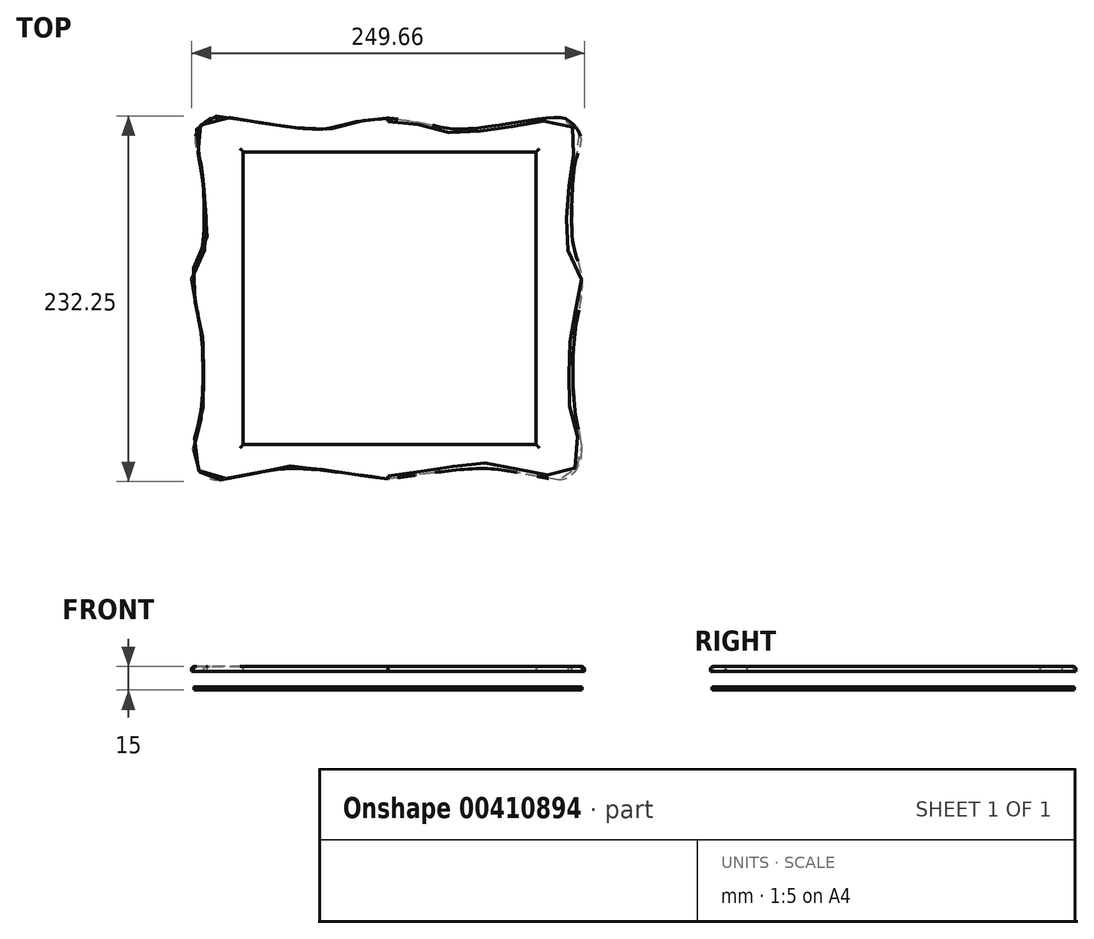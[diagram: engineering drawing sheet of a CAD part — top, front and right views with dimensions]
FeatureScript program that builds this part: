
annotation { "Feature Type Name" : "Feature", "Feature Type Description" : "" }
export const myFeature = defineFeature(function(context is Context, id is Id, definition is map)
    precondition{}
    {
        {
            var Q0;
            Q0=qCreatedBy(makeId("Top.planeOp"),FACE);
            var sketch = newSketch(context, id + "F0", { "sketchPlane" : qUnion([Q0])});
            skLineSegment(sketch, "E0.bottom", {"start": v(-122.5, 118.1) * mm, "end": v(122.5, 118.1) * mm, "construction": true});
            skLineSegment(sketch, "E0.top", {"start": v(-122.5, -111.11) * mm, "end": v(122.5, -111.11) * mm, "construction": true});
            skLineSegment(sketch, "E0.left", {"start": v(-122.5, 118.1) * mm, "end": v(-122.5, -111.11) * mm, "construction": true});
            skLineSegment(sketch, "E0.right", {"start": v(122.5, 118.1) * mm, "end": v(122.5, -111.11) * mm, "construction": true});
            skFitSpline(sketch, "E1", {"points": [v(0, 118.1) * mm, v(20.88, 115.2) * mm, v(36.99, 111.75) * mm, v(45.47, 111.22) * mm, v(51.55, 111.37) * mm, v(59.29, 112.14) * mm, v(75.33, 114.44) * mm, v(99.86, 118.1) * mm, v(111.75, 118.1) * mm, v(117.88, 114.06) * mm, v(122.5, 105.24) * mm, v(119.42, 91.82) * mm, v(117.12, 71.88) * mm, v(117.88, 37) * mm, v(122.5, 20.89) * mm, v(122.5, 3.5) * mm, v(119.03, -16.3) * mm, v(117.5, -40.46) * mm, v(119.03, -69.6) * mm, v(122.5, -87.23) * mm, v(122.5, -97.2) * mm, v(119.42, -105.25) * mm, v(112.52, -111.11) * mm, v(104.08, -111.11) * mm, v(84.91, -107.55) * mm, v(62.3, -104.48) * mm, v(31.62, -106.78) * mm, v(17.8, -108.62) * mm, v(0, -111.11) * mm], "startDerivative": vector(493.95, -54.97) * mm, "endDerivative": vector(-585.5, -82.83) * mm});
            skFitSpline(sketch, "E2.MirrorCS", {"points": [v(0, 118.1) * mm, v(-20.88, 115.2) * mm, v(-36.99, 111.75) * mm, v(-45.47, 111.22) * mm, v(-51.55, 111.37) * mm, v(-59.29, 112.14) * mm, v(-75.33, 114.44) * mm, v(-99.86, 118.1) * mm, v(-111.75, 118.1) * mm, v(-117.88, 114.06) * mm, v(-122.5, 105.24) * mm, v(-119.42, 91.82) * mm, v(-117.12, 71.88) * mm, v(-117.88, 37) * mm, v(-122.5, 20.89) * mm, v(-122.5, 3.5) * mm, v(-119.03, -16.3) * mm, v(-117.5, -40.46) * mm, v(-119.03, -69.6) * mm, v(-122.5, -87.23) * mm, v(-122.5, -97.2) * mm, v(-119.42, -105.25) * mm, v(-112.52, -111.11) * mm, v(-104.08, -111.11) * mm, v(-84.91, -107.55) * mm, v(-62.3, -104.48) * mm, v(-31.62, -106.78) * mm, v(-17.8, -108.62) * mm, v(0, -111.11) * mm], "startDerivative": vector(-493.95, -54.97) * mm, "endDerivative": vector(585.5, -82.83) * mm});
            skSolve(sketch);
        }
        {
            var Q0;
            Q0=makeQuery(id+"F0.imprint","IMPRINT",FACE,{"disambiguationData":[TD([[makeQuery(id+"F0.imprint","IMPRINT",EDGE,{"derivedFrom":sQuery(id+"F0.wireOp",EDGE,"E1")}),-1.0]])]});
            extrude(context, id + "F1", {"entities" : qUnion([Q0]), "depth" : 2 * mm});
        }
        {
            var Q0;
            Q0=makeQuery(id+"F1.opExtrude","CAP_FACE",FACE,{"disambiguationData":[OSD([sQuery(id+"F0.wireOp",EDGE,"E1"),sQuery(id+"F0.wireOp",EDGE,"E2.MirrorCS")])],"isStart":false});
            cPlane(context, id + "F2", {"entities" : qUnion([Q0]), "cplaneType" : CPlaneType.OFFSET, "offset" : 10 * mm, "width" : 150 * mm, "height" : 150 * mm});
        }
        {
            var Q0;
            Q0=qCreatedBy(id+"F2.planeOp",FACE);
            var sketch = newSketch(context, id + "F3", { "sketchPlane" : qUnion([Q0])});
            skFitSpline(sketch, "E3.0.0", {"points": [v(0, -111.11) * mm, v(7.44, -110.06) * mm, v(17.73, -108.63) * mm, v(31.7, -106.71) * mm, v(63, -103) * mm, v(83.84, -107.42) * mm, v(103.65, -111.14) * mm, v(112.63, -112.41) * mm, v(120.18, -105.53) * mm, v(123, -97.14) * mm, v(123.05, -86.58) * mm, v(117.91, -69.16) * mm, v(117.16, -40.36) * mm, v(118.29, -16.58) * mm, v(123.07, 3) * mm, v(123.82, 21.64) * mm, v(115.75, 36.55) * mm, v(117.02, 72.12) * mm, v(118.13, 91.04) * mm, v(124.7, 105.08) * mm, v(118.21, 114.4) * mm, v(111.75, 119.18) * mm, v(99.23, 118.3) * mm, v(75.58, 114.4) * mm, v(59.86, 112.14) * mm, v(51.7, 111.28) * mm, v(45.3, 111.18) * mm, v(36.45, 111.31) * mm, v(20.57, 115.82) * mm, v(6.8, 117.34) * mm, v(0, 118.1) * mm]});
            skFitSpline(sketch, "E3.0.1", {"points": [v(0, 118.1) * mm, v(-6.8, 117.34) * mm, v(-20.57, 115.82) * mm, v(-36.45, 111.31) * mm, v(-45.3, 111.18) * mm, v(-51.7, 111.28) * mm, v(-59.86, 112.14) * mm, v(-75.58, 114.4) * mm, v(-99.23, 118.3) * mm, v(-111.75, 119.18) * mm, v(-118.21, 114.4) * mm, v(-124.7, 105.08) * mm, v(-118.13, 91.04) * mm, v(-117.02, 72.12) * mm, v(-115.75, 36.55) * mm, v(-123.82, 21.64) * mm, v(-123.07, 3) * mm, v(-118.29, -16.58) * mm, v(-117.16, -40.36) * mm, v(-117.91, -69.16) * mm, v(-123.05, -86.58) * mm, v(-123, -97.14) * mm, v(-120.18, -105.53) * mm, v(-112.63, -112.41) * mm, v(-103.65, -111.14) * mm, v(-83.84, -107.42) * mm, v(-63, -103) * mm, v(-31.7, -106.71) * mm, v(-17.73, -108.63) * mm, v(-7.44, -110.06) * mm, v(0, -111.11) * mm]});
            skSolve(sketch);
        }
        {
            var Q0;
            Q0=makeQuery(id+"F3.imprint","IMPRINT",FACE,{"disambiguationData":[TD([[makeQuery(id+"F3.imprint","IMPRINT",EDGE,{"derivedFrom":sQuery(id+"F3.wireOp",EDGE,"E3.0.0")}),1.0]])]});
            extrude(context, id + "F4", {"entities" : qUnion([Q0]), "depth" : 3 * mm});
        }
        {
            var Q0;
            Q0=qCreatedBy(id+"F2.planeOp",FACE);
            cPlane(context, id + "F5", {"entities" : qUnion([Q0]), "cplaneType" : CPlaneType.OFFSET, "offset" : 5 * mm, "width" : 150 * mm, "height" : 150 * mm});
        }
        {
            var Q0;
            Q0=qCreatedBy(id+"F5.planeOp",FACE);
            var sketch = newSketch(context, id + "F6", { "sketchPlane" : qUnion([Q0])});
            skLineSegment(sketch, "E4.0", {"start": v(-91.85, 96.66) * mm, "end": v(94.15, 96.66) * mm});
            skLineSegment(sketch, "E5.0", {"start": v(-91.85, 96.66) * mm, "end": v(-91.85, -89.34) * mm});
            skLineSegment(sketch, "E6.0", {"start": v(-91.85, -89.34) * mm, "end": v(94.15, -89.34) * mm});
            skLineSegment(sketch, "E7.0", {"start": v(94.15, 96.66) * mm, "end": v(94.15, -89.34) * mm});
            skSolve(sketch);
        }
        {
            var Q0;
            Q0=qSketchRegion(id+"F6",true);
            extrude(context, id + "F7", {"entities" : qUnion([Q0]), "operationType" : NewBodyOperationType.REMOVE, "oppositeDirection" : true, "depth" : 10.5 * mm});
        }
        {
            var Q0;
            Q0=makeQuery(id+"F4.opExtrude","CAP_FACE",FACE,{"disambiguationData":[OSD([sQuery(id+"F3.wireOp",EDGE,"E3.0.0"),sQuery(id+"F3.wireOp",EDGE,"E3.0.1")])],"isStart":false});
            fillet(context, id + "F8", {"entities" : qUnion([Q0]), "radius" : 2 * mm, "tangentPropagation" : true, "allowEdgeOverflow" : false});
        }
    });
